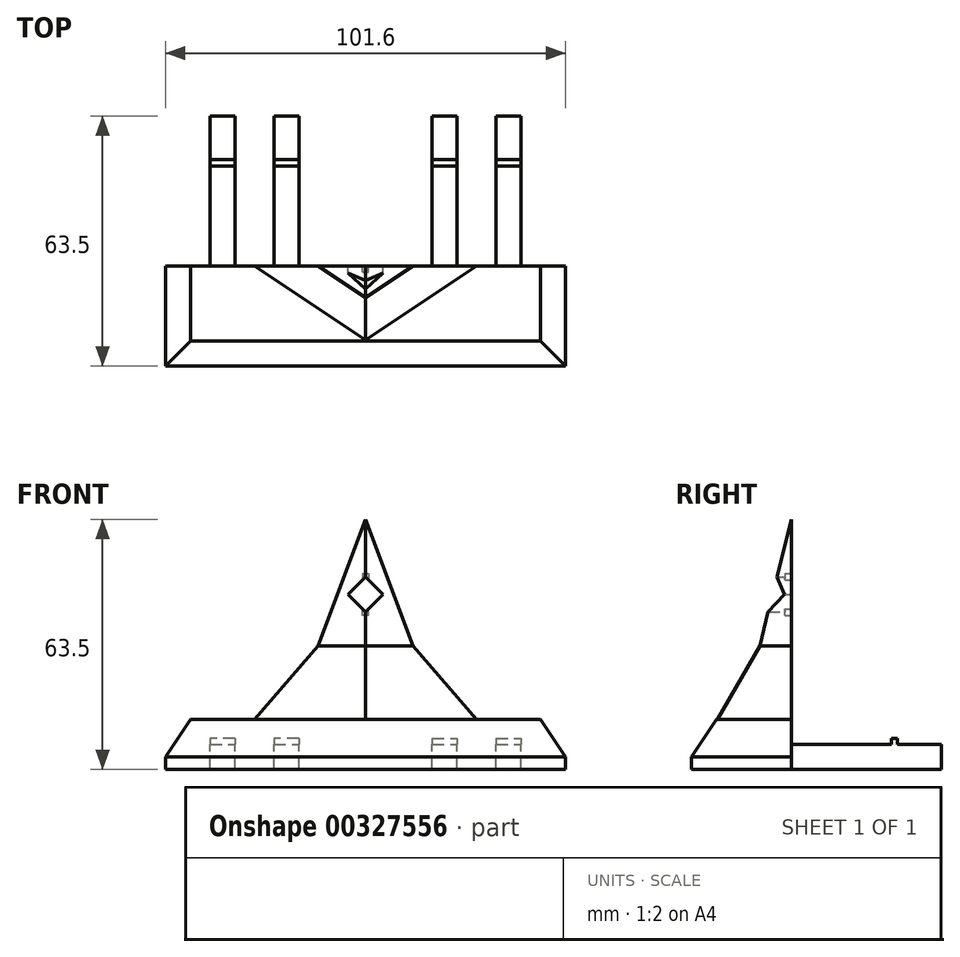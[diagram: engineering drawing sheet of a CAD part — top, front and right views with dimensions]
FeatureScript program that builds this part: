
annotation { "Feature Type Name" : "Feature", "Feature Type Description" : "" }
export const myFeature = defineFeature(function(context is Context, id is Id, definition is map)
    precondition{}
    {
        {
            var Q0;
            Q0=qCreatedBy(makeId("Top.planeOp"),FACE);
            var sketch = newSketch(context, id + "F0", { "sketchPlane" : qUnion([Q0])});
            skLineSegment(sketch, "E0.bottom", {"start": v(50.8, -25.4) * mm, "end": v(-50.8, -25.4) * mm});
            skLineSegment(sketch, "E0.top", {"start": v(50.8, 0) * mm, "end": v(-50.8, 0) * mm});
            skLineSegment(sketch, "E0.left", {"start": v(50.8, -25.4) * mm, "end": v(50.8, 0) * mm});
            skLineSegment(sketch, "E0.right", {"start": v(-50.8, -25.4) * mm, "end": v(-50.8, 0) * mm});
            skPoint(sketch, "E0.middle", {"position": v(0, -12.7) * mm});
            skSolve(sketch);
        }
        {
            var Q0;
            Q0 = qSketchRegion(id + "F0", true);
            extrude(context, id + "F1", {"entities" : qUnion([Q0]), "depth" : 12.7 * mm});
        }
        {
            var Q0;
            Q0=makeQuery(id+"F1.opExtrude","CAP_EDGE",EDGE,{"disambiguationData":[OSD([sQuery(id+"F0.wireOp",EDGE,"E0.bottom")])],"isStart":false});
            var Q1;
            Q1=makeQuery(id+"F1.opExtrude","CAP_EDGE",EDGE,{"disambiguationData":[OSD([sQuery(id+"F0.wireOp",EDGE,"E0.right")])],"isStart":false});
            var Q2;
            Q2=makeQuery(id+"F1.opExtrude","CAP_EDGE",EDGE,{"disambiguationData":[OSD([sQuery(id+"F0.wireOp",EDGE,"E0.left")])],"isStart":false});
            chamfer(context, id + "F2", {"entities" : qUnion([Q0, Q1, Q2]), "chamferType" : ChamferType.TWO_OFFSETS, "width1" : 9.52 * mm, "oppositeDirection" : false, "width2" : 6.35 * mm, "tangentPropagation" : true});
        }
        {
            var Q0;
            Q0=qCreatedBy(makeId("Front.planeOp"),FACE);
            var sketch = newSketch(context, id + "F3", { "sketchPlane" : qUnion([Q0])});
            skLineSegment(sketch, "E1", {"start": v(-19.05, 12.7) * mm, "end": v(0, 63.5) * mm});
            skLineSegment(sketch, "E2", {"start": v(0, 63.5) * mm, "end": v(19.05, 12.7) * mm});
            skLineSegment(sketch, "E3", {"start": v(-19.05, 12.7) * mm, "end": v(19.05, 12.7) * mm});
            skSolve(sketch);
        }
        {
            var Q0;
            Q0 = qSketchRegion(id + "F3", true);
            extrude(context, id + "F4", {"entities" : qUnion([Q0]), "operationType" : NewBodyOperationType.ADD, "depth" : 12.7 * mm});
        }
        {
            var Q0;
            Q0=makeQuery(id+"F4.opExtrude","CAP_EDGE",EDGE,{"disambiguationData":[OSD([sQuery(id+"F3.wireOp",EDGE,"E2")])],"isStart":false});
            var Q1;
            Q1=makeQuery(id+"F4.opExtrude","CAP_EDGE",EDGE,{"disambiguationData":[OSD([sQuery(id+"F3.wireOp",EDGE,"E1")])],"isStart":false});
            chamfer(context, id + "F5", {"entities" : qUnion([Q0, Q1]), "chamferType" : ChamferType.TWO_OFFSETS, "width1" : 12.7 * mm, "oppositeDirection" : false, "width2" : 17.78 * mm, "tangentPropagation" : true});
        }
        {
            var Q0;
            Q0=makeQuery(id+"F5.opChamfer","BLEND_EDGE",EDGE,{"blendedFrom":[makeQuery(id+"F4.opExtrude","CAP_EDGE",EDGE,{"disambiguationData":[OSD([sQuery(id+"F3.wireOp",EDGE,"E2")])],"isStart":false}),makeQuery(id+"F1.opExtrude","CAP_FACE",FACE,{"disambiguationData":[OSD([sQuery(id+"F0.wireOp",EDGE,"E0.bottom"),sQuery(id+"F0.wireOp",EDGE,"E0.top"),sQuery(id+"F0.wireOp",EDGE,"E0.left"),sQuery(id+"F0.wireOp",EDGE,"E0.right")])],"isStart":false})],"blendedInto":[makeQuery(id+"F1.opExtrude","CAP_FACE",FACE,{"disambiguationData":[OSD([sQuery(id+"F0.wireOp",EDGE,"E0.bottom"),sQuery(id+"F0.wireOp",EDGE,"E0.top"),sQuery(id+"F0.wireOp",EDGE,"E0.left"),sQuery(id+"F0.wireOp",EDGE,"E0.right")])],"isStart":false})]});
            var Q1;
            Q1=makeQuery(id+"F5.opChamfer","BLEND_EDGE",EDGE,{"blendedFrom":[makeQuery(id+"F4.opExtrude","CAP_EDGE",EDGE,{"disambiguationData":[OSD([sQuery(id+"F3.wireOp",EDGE,"E1")])],"isStart":false}),makeQuery(id+"F1.opExtrude","CAP_FACE",FACE,{"disambiguationData":[OSD([sQuery(id+"F0.wireOp",EDGE,"E0.bottom"),sQuery(id+"F0.wireOp",EDGE,"E0.top"),sQuery(id+"F0.wireOp",EDGE,"E0.left"),sQuery(id+"F0.wireOp",EDGE,"E0.right")])],"isStart":false})],"blendedInto":[makeQuery(id+"F1.opExtrude","CAP_FACE",FACE,{"disambiguationData":[OSD([sQuery(id+"F0.wireOp",EDGE,"E0.bottom"),sQuery(id+"F0.wireOp",EDGE,"E0.top"),sQuery(id+"F0.wireOp",EDGE,"E0.left"),sQuery(id+"F0.wireOp",EDGE,"E0.right")])],"isStart":false})]});
            chamfer(context, id + "F6", {"entities" : qUnion([Q0, Q1]), "chamferType" : ChamferType.TWO_OFFSETS, "width1" : 19.05 * mm, "oppositeDirection" : true, "width2" : 5.08 * mm, "tangentPropagation" : true});
        }
        {
            var Q0;
            Q0=makeQuery(id+"F4.boolean.opBoolean","MERGE",FACE,{"derivedFrom":[makeQuery(id+"F1.opExtrude","SWEPT_FACE",FACE,{"disambiguationData":[OSD([sQuery(id+"F0.wireOp",EDGE,"E0.top")])]}),makeQuery(id+"F4.opExtrude","CAP_FACE",FACE,{"disambiguationData":[OSD([sQuery(id+"F3.wireOp",EDGE,"E1"),sQuery(id+"F3.wireOp",EDGE,"E2"),sQuery(id+"F3.wireOp",EDGE,"E3")])],"isStart":true})]});
            var sketch = newSketch(context, id + "F7", { "sketchPlane" : qUnion([Q0])});
            skLineSegment(sketch, "E4.bottom", {"start": v(-33.14, 0) * mm, "end": v(-39.5, 0) * mm});
            skLineSegment(sketch, "E4.top", {"start": v(-33.14, 6.35) * mm, "end": v(-39.5, 6.35) * mm});
            skLineSegment(sketch, "E4.left", {"start": v(-33.14, 0) * mm, "end": v(-33.14, 6.35) * mm});
            skLineSegment(sketch, "E4.right", {"start": v(-39.5, 0) * mm, "end": v(-39.5, 6.35) * mm});
            skPoint(sketch, "E4.middle", {"position": v(-36.32, 3.17) * mm});
            skPoint(sketch, "E4.middle.positionSnap0", {"position": v(-36.32, 12.7) * mm});
            skPoint(sketch, "E4.centerSnap0", {"position": v(-36.32, 12.7) * mm});
            skLineSegment(sketch, "E5.bottom", {"start": v(39.5, 0) * mm, "end": v(33.14, 0) * mm});
            skLineSegment(sketch, "E5.top", {"start": v(39.5, 6.35) * mm, "end": v(33.14, 6.35) * mm});
            skLineSegment(sketch, "E5.left", {"start": v(39.5, 0) * mm, "end": v(39.5, 6.35) * mm});
            skLineSegment(sketch, "E5.right", {"start": v(33.14, 0) * mm, "end": v(33.14, 6.35) * mm});
            skPoint(sketch, "E5.middle", {"position": v(36.32, 3.17) * mm});
            skPoint(sketch, "E5.middle.positionSnap0", {"position": v(36.32, 12.7) * mm});
            skPoint(sketch, "E5.centerSnap0", {"position": v(36.32, 12.7) * mm});
            skLineSegment(sketch, "E6.bottom", {"start": v(-16.95, 0) * mm, "end": v(-23.3, 0) * mm});
            skLineSegment(sketch, "E6.top", {"start": v(-16.95, 6.35) * mm, "end": v(-23.3, 6.35) * mm});
            skLineSegment(sketch, "E6.left", {"start": v(-16.95, 0) * mm, "end": v(-16.95, 6.35) * mm});
            skLineSegment(sketch, "E6.right", {"start": v(-23.3, 0) * mm, "end": v(-23.3, 6.35) * mm});
            skPoint(sketch, "E6.middle", {"position": v(-20.12, 3.17) * mm});
            skPoint(sketch, "E6.middle.positionSnap0", {"position": v(-33.14, 3.17) * mm});
            skPoint(sketch, "E6.middle.positionSnap1", {"position": v(-20.12, 22.02) * mm});
            skPoint(sketch, "E6.centerSnap0", {"position": v(-33.14, 3.17) * mm});
            skPoint(sketch, "E6.centerSnap1", {"position": v(-20.12, 22.02) * mm});
            skLineSegment(sketch, "E7.bottom", {"start": v(23.3, 0) * mm, "end": v(16.95, 0) * mm});
            skLineSegment(sketch, "E7.top", {"start": v(23.3, 6.35) * mm, "end": v(16.95, 6.35) * mm});
            skLineSegment(sketch, "E7.left", {"start": v(23.3, 0) * mm, "end": v(23.3, 6.35) * mm});
            skLineSegment(sketch, "E7.right", {"start": v(16.95, 0) * mm, "end": v(16.95, 6.35) * mm});
            skPoint(sketch, "E7.middle", {"position": v(20.12, 3.17) * mm});
            skPoint(sketch, "E7.middle.positionSnap0", {"position": v(33.14, 3.17) * mm});
            skPoint(sketch, "E7.middle.positionSnap1", {"position": v(20.12, 22.02) * mm});
            skPoint(sketch, "E7.centerSnap0", {"position": v(33.14, 3.17) * mm});
            skPoint(sketch, "E7.centerSnap1", {"position": v(20.12, 22.02) * mm});
            skSolve(sketch);
        }
        {
            var Q0;
            Q0 = qSketchRegion(id + "F7", true);
            extrude(context, id + "F8", {"entities" : qUnion([Q0]), "operationType" : NewBodyOperationType.ADD, "depth" : 38.1 * mm});
        }
        {
            var Q0;
            Q0=makeQuery(id+"F8.opExtrude","SWEPT_FACE",FACE,{"disambiguationData":[OSD([sQuery(id+"F7.wireOp",EDGE,"E7.top")])]});
            var sketch = newSketch(context, id + "F9", { "sketchPlane" : qUnion([Q0])});
            skLineSegment(sketch, "E8.bottom", {"start": v(-16.95, 26.99) * mm, "end": v(-23.3, 26.99) * mm});
            skLineSegment(sketch, "E8.top", {"start": v(-16.95, 25.4) * mm, "end": v(-23.3, 25.4) * mm});
            skLineSegment(sketch, "E8.left", {"start": v(-16.95, 26.99) * mm, "end": v(-16.95, 25.4) * mm});
            skLineSegment(sketch, "E8.right", {"start": v(-23.3, 26.99) * mm, "end": v(-23.3, 25.4) * mm});
            skPoint(sketch, "E8.middle", {"position": v(-20.12, 26.2) * mm});
            skPoint(sketch, "E8.middle.positionSnap0", {"position": v(-20.12, 38.1) * mm});
            skPoint(sketch, "E8.middle.positionSnap1", {"position": v(-16.95, 26.2) * mm});
            skPoint(sketch, "E8.centerSnap0", {"position": v(-20.12, 38.1) * mm});
            skPoint(sketch, "E8.centerSnap1", {"position": v(-16.95, 26.2) * mm});
            skLineSegment(sketch, "E9.bottom", {"start": v(-33.14, 25.4) * mm, "end": v(-39.5, 25.4) * mm});
            skLineSegment(sketch, "E9.top", {"start": v(-33.14, 26.99) * mm, "end": v(-39.5, 26.99) * mm});
            skLineSegment(sketch, "E9.left", {"start": v(-33.14, 25.4) * mm, "end": v(-33.14, 26.99) * mm});
            skLineSegment(sketch, "E9.right", {"start": v(-39.5, 25.4) * mm, "end": v(-39.5, 26.99) * mm});
            skPoint(sketch, "E9.middle", {"position": v(-36.32, 26.2) * mm});
            skLineSegment(sketch, "E10.bottom", {"start": v(16.95, 25.4) * mm, "end": v(23.3, 25.4) * mm});
            skLineSegment(sketch, "E10.top", {"start": v(16.95, 26.99) * mm, "end": v(23.3, 26.99) * mm});
            skLineSegment(sketch, "E10.left", {"start": v(16.95, 25.4) * mm, "end": v(16.95, 26.99) * mm});
            skLineSegment(sketch, "E10.right", {"start": v(23.3, 25.4) * mm, "end": v(23.3, 26.99) * mm});
            skPoint(sketch, "E10.middle", {"position": v(20.12, 26.2) * mm});
            skLineSegment(sketch, "E11.bottom", {"start": v(33.14, 25.4) * mm, "end": v(39.5, 25.4) * mm});
            skLineSegment(sketch, "E11.top", {"start": v(33.14, 26.99) * mm, "end": v(39.5, 26.99) * mm});
            skLineSegment(sketch, "E11.left", {"start": v(33.14, 25.4) * mm, "end": v(33.14, 26.99) * mm});
            skLineSegment(sketch, "E11.right", {"start": v(39.5, 25.4) * mm, "end": v(39.5, 26.99) * mm});
            skPoint(sketch, "E11.middle", {"position": v(36.32, 26.2) * mm});
            skSolve(sketch);
        }
        {
            var Q0;
            Q0 = qSketchRegion(id + "F9", true);
            extrude(context, id + "F10", {"entities" : qUnion([Q0]), "operationType" : NewBodyOperationType.ADD, "depth" : 1.59 * mm});
        }
        {
            var Q0;
            Q0=makeQuery(id+"F4.boolean.opBoolean","MERGE",FACE,{"derivedFrom":[makeQuery(id+"F1.opExtrude","SWEPT_FACE",FACE,{"disambiguationData":[OSD([sQuery(id+"F0.wireOp",EDGE,"E0.top")])]}),makeQuery(id+"F4.opExtrude","CAP_FACE",FACE,{"disambiguationData":[OSD([sQuery(id+"F3.wireOp",EDGE,"E1"),sQuery(id+"F3.wireOp",EDGE,"E2"),sQuery(id+"F3.wireOp",EDGE,"E3")])],"isStart":true})]});
            var sketch = newSketch(context, id + "F11", { "sketchPlane" : qUnion([Q0])});
            skLineSegment(sketch, "E12.bottom", {"start": v(4.5, 44.45) * mm, "end": v(0, 39.96) * mm});
            skLineSegment(sketch, "E12.top", {"start": v(0, 48.94) * mm, "end": v(-4.5, 44.45) * mm});
            skLineSegment(sketch, "E12.left", {"start": v(4.5, 44.45) * mm, "end": v(0, 48.94) * mm});
            skLineSegment(sketch, "E12.right", {"start": v(0, 39.96) * mm, "end": v(-4.5, 44.45) * mm});
            skPoint(sketch, "E12.middle", {"position": v(0, 44.45) * mm});
            skLineSegment(sketch, "E13.bottom", {"start": v(-0.8, 39.17) * mm, "end": v(0.8, 39.17) * mm});
            skLineSegment(sketch, "E13.top", {"start": v(-0.8, 40.75) * mm, "end": v(0.8, 40.75) * mm});
            skLineSegment(sketch, "E13.left", {"start": v(-0.8, 39.17) * mm, "end": v(-0.8, 40.75) * mm});
            skLineSegment(sketch, "E13.right", {"start": v(0.8, 39.17) * mm, "end": v(0.8, 40.75) * mm});
            skPoint(sketch, "E13.middle", {"position": v(0, 39.96) * mm});
            skLineSegment(sketch, "E14.bottom", {"start": v(0.8, 49.73) * mm, "end": v(-0.8, 49.73) * mm});
            skLineSegment(sketch, "E14.top", {"start": v(0.8, 48.15) * mm, "end": v(-0.8, 48.15) * mm});
            skLineSegment(sketch, "E14.left", {"start": v(0.8, 49.73) * mm, "end": v(0.8, 48.15) * mm});
            skLineSegment(sketch, "E14.right", {"start": v(-0.8, 49.73) * mm, "end": v(-0.8, 48.15) * mm});
            skPoint(sketch, "E14.middle", {"position": v(0, 48.94) * mm});
            skSolve(sketch);
        }
        {
            var Q0;
            Q0=makeQuery(id+"F11.imprint","IMPRINT",FACE,{"disambiguationData":[TD([[makeQuery(id+"F11.imprint","IMPRINT",EDGE,{"derivedFrom":sQuery(id+"F11.wireOp",EDGE,"E12.bottom")}),-1.0]])]});
            var Q1;
            {var subQ3=sQuery(id+"F11.wireOp",EDGE,"E13.top");Q1=makeQuery(id+"F11.imprint","IMPRINT",FACE,{"disambiguationData":[TD([[makeQuery(id+"F11.imprint","IMPRINT",EDGE,{"derivedFrom":subQ3}),1.0]])]});}
            var Q2;
            {var subQ3=sQuery(id+"F11.wireOp",EDGE,"E14.top");Q2=makeQuery(id+"F11.imprint","IMPRINT",FACE,{"disambiguationData":[TD([[makeQuery(id+"F11.imprint","IMPRINT",EDGE,{"derivedFrom":subQ3}),-1.0]])]});}
            extrude(context, id + "F12", {"entities" : qUnion([Q0, Q1, Q2]), "operationType" : NewBodyOperationType.REMOVE, "oppositeDirection" : true, "depth" : 25.4 * mm});
        }
        {
            var Q0;
            Q0=makeQuery(id+"F11.imprint","IMPRINT",FACE,{"disambiguationData":[TD([[makeQuery(id+"F11.imprint","IMPRINT",EDGE,{"derivedFrom":sQuery(id+"F11.wireOp",EDGE,"E14.bottom")}),1.0]])]});
            var Q1;
            Q1=makeQuery(id+"F11.imprint","IMPRINT",FACE,{"disambiguationData":[TD([[makeQuery(id+"F11.imprint","IMPRINT",EDGE,{"derivedFrom":sQuery(id+"F11.wireOp",EDGE,"E13.bottom")}),1.0]])]});
            extrude(context, id + "F13", {"entities" : qUnion([Q0, Q1]), "operationType" : NewBodyOperationType.REMOVE, "oppositeDirection" : true, "depth" : 1.59 * mm});
        }
    });
